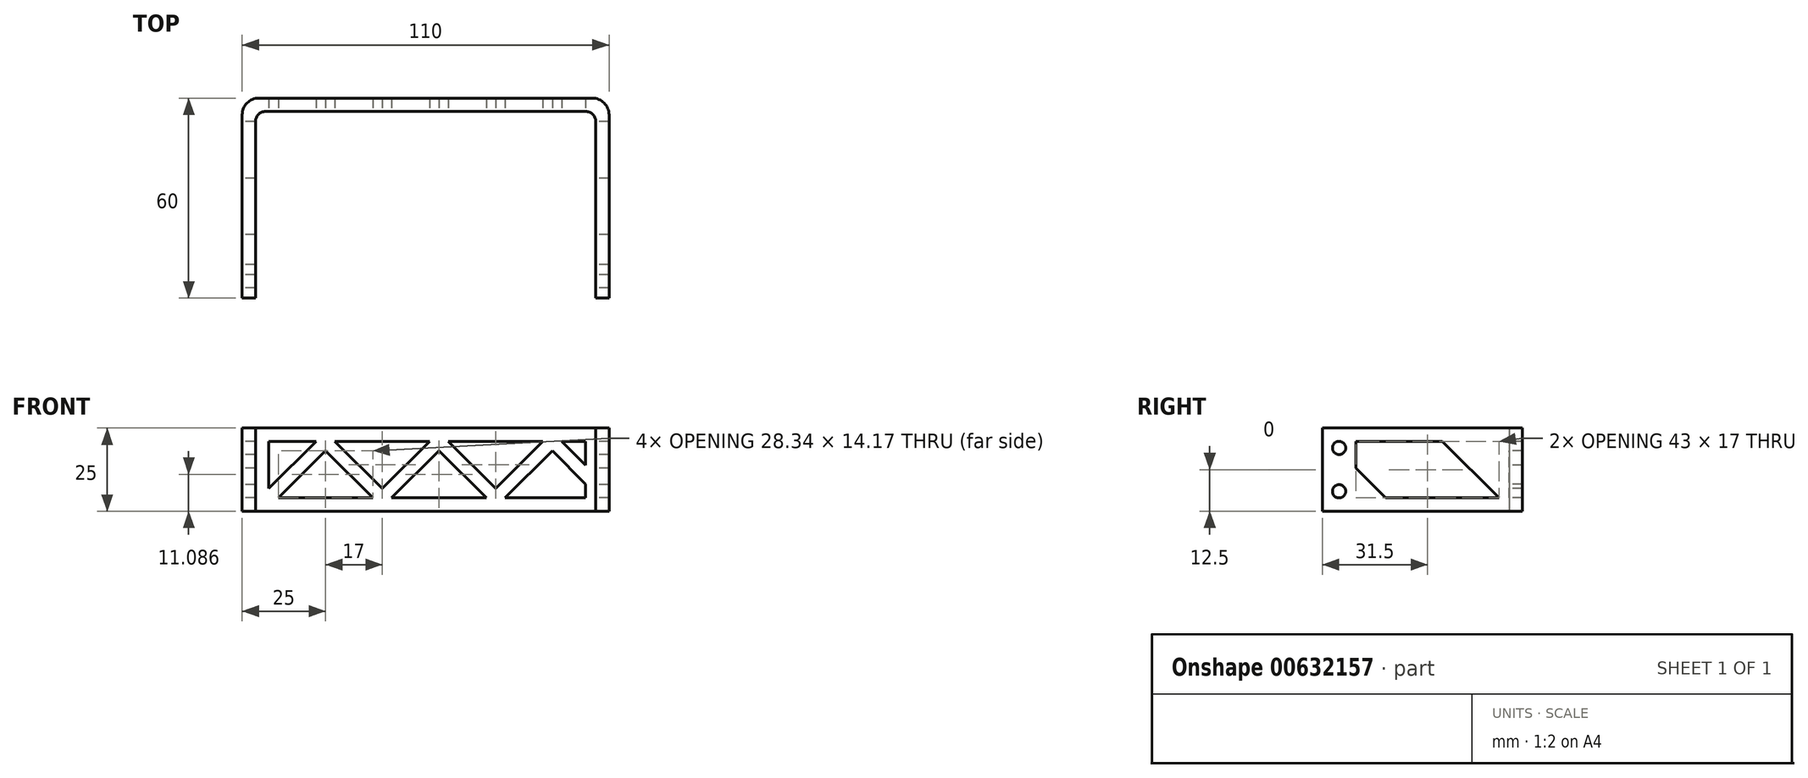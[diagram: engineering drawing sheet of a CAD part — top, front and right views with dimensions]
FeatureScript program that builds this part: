
annotation { "Feature Type Name" : "Feature", "Feature Type Description" : "" }
export const myFeature = defineFeature(function(context is Context, id is Id, definition is map)
    precondition{}
    {
        {
            var Q0;
            Q0=qCreatedBy(makeId("Top.planeOp"),FACE);
            var sketch = newSketch(context, id + "F0", { "sketchPlane" : qUnion([Q0])});
            skLineSegment(sketch, "E0", {"start": v(0, 0) * mm, "end": v(0, 53) * mm});
            skLineSegment(sketch, "E1", {"start": v(-3, 56) * mm, "end": v(-99, 56) * mm});
            skLineSegment(sketch, "E2", {"start": v(-102, 53) * mm, "end": v(-102, 0) * mm});
            skLineSegment(sketch, "E3.0", {"start": v(-106, 55) * mm, "end": v(-106, 0) * mm});
            skLineSegment(sketch, "E3.1", {"start": v(-1, 60) * mm, "end": v(-101, 60) * mm});
            skLineSegment(sketch, "E3.2", {"start": v(4, 0) * mm, "end": v(4, 55) * mm});
            skLineSegment(sketch, "E4.bottom", {"start": v(-106, 0) * mm, "end": v(-102, 0) * mm});
            skLineSegment(sketch, "E5", {"start": v(4, 0) * mm, "end": v(0, 0) * mm});
            skPoint(sketch, "E6.visualSharp", {"position": v(-102, 56) * mm});
            skArc(sketch, "E6.filletArc", {"start": v(-99, 56) * mm, "mid": v(-101.12, 55.12) * mm, "end": v(-102, 53) * mm});
            skPoint(sketch, "E7.visualSharp", {"position": v(0, 56) * mm});
            skArc(sketch, "E7.filletArc", {"start": v(0, 53) * mm, "mid": v(-0.88, 55.12) * mm, "end": v(-3, 56) * mm});
            skPoint(sketch, "E8.visualSharp", {"position": v(-106, 60) * mm});
            skArc(sketch, "E8.filletArc", {"start": v(-101, 60) * mm, "mid": v(-104.54, 58.54) * mm, "end": v(-106, 55) * mm});
            skPoint(sketch, "E9.visualSharp", {"position": v(4, 60) * mm});
            skArc(sketch, "E9.filletArc", {"start": v(4, 55) * mm, "mid": v(2.54, 58.54) * mm, "end": v(-1, 60) * mm});
            skSolve(sketch);
        }
        {
            var Q0;
            Q0=makeQuery(id+"F0.imprint","IMPRINT",FACE,{"disambiguationData":[TD([[makeQuery(id+"F0.imprint","IMPRINT",EDGE,{"derivedFrom":sQuery(id+"F0.wireOp",EDGE,"E0")}),-1.0]])]});
            extrude(context, id + "F1", {"entities" : qUnion([Q0]), "depth" : 25 * mm, "offsetDistance" : 25 * mm});
        }
        {
            var Q0;
            Q0=makeQuery(id+"F1.opExtrude","SWEPT_FACE",FACE,{"disambiguationData":[OSD([sQuery(id+"F0.wireOp",EDGE,"E1")])]});
            var sketch = newSketch(context, id + "F2", { "sketchPlane" : qUnion([Q0])});
            skLineSegment(sketch, "E10", {"start": v(-98, 4) * mm, "end": v(-81, 21) * mm, "construction": true});
            skLineSegment(sketch, "E11", {"start": v(-81, 21) * mm, "end": v(-64, 4) * mm, "construction": true});
            skLineSegment(sketch, "E12", {"start": v(-64, 4) * mm, "end": v(-47, 21) * mm, "construction": true});
            skLineSegment(sketch, "E13", {"start": v(-47, 21) * mm, "end": v(-30, 4) * mm, "construction": true});
            skLineSegment(sketch, "E14", {"start": v(-64, 4) * mm, "end": v(-116.6, 4) * mm, "construction": true});
            skLineSegment(sketch, "E15", {"start": v(-81, 21) * mm, "end": v(-144.6, 21) * mm, "construction": true});
            skLineSegment(sketch, "E16", {"start": v(-64, 4) * mm, "end": v(16.38, 4) * mm, "construction": true});
            skLineSegment(sketch, "E17", {"start": v(-30, 4) * mm, "end": v(-13, 21) * mm, "construction": true});
            skLineSegment(sketch, "E18", {"start": v(-13, 21) * mm, "end": v(-3, 11) * mm, "construction": true});
            skLineSegment(sketch, "E19.0", {"start": v(-13, 18.17) * mm, "end": v(-4.41, 9.59) * mm});
            skLineSegment(sketch, "E19.1", {"start": v(-30, 1.17) * mm, "end": v(-13, 18.17) * mm});
            skLineSegment(sketch, "E19.2", {"start": v(-96.59, 2.59) * mm, "end": v(-81, 18.17) * mm});
            skLineSegment(sketch, "E19.3", {"start": v(-81, 18.17) * mm, "end": v(-64, 1.17) * mm});
            skLineSegment(sketch, "E19.4", {"start": v(-64, 1.17) * mm, "end": v(-47, 18.17) * mm});
            skLineSegment(sketch, "E19.5", {"start": v(-47, 18.17) * mm, "end": v(-30, 1.17) * mm});
            skLineSegment(sketch, "E20.0", {"start": v(-13, 23.83) * mm, "end": v(-1.59, 12.41) * mm});
            skLineSegment(sketch, "E20.1", {"start": v(-30, 6.83) * mm, "end": v(-13, 23.83) * mm});
            skLineSegment(sketch, "E20.2", {"start": v(-99.41, 5.41) * mm, "end": v(-81, 23.83) * mm});
            skLineSegment(sketch, "E20.3", {"start": v(-81, 23.83) * mm, "end": v(-64, 6.83) * mm});
            skLineSegment(sketch, "E20.4", {"start": v(-64, 6.83) * mm, "end": v(-47, 23.83) * mm});
            skLineSegment(sketch, "E20.5", {"start": v(-47, 23.83) * mm, "end": v(-30, 6.83) * mm});
            skLineSegment(sketch, "E21", {"start": v(-98, 4) * mm, "end": v(-64, 4) * mm});
            skLineSegment(sketch, "E22", {"start": v(-30, 4) * mm, "end": v(-3, 4) * mm});
            skLineSegment(sketch, "E23", {"start": v(-3, 4) * mm, "end": v(-3, 11) * mm});
            skLineSegment(sketch, "E24", {"start": v(-81, 21) * mm, "end": v(-47, 21) * mm});
            skLineSegment(sketch, "E25", {"start": v(-13, 21) * mm, "end": v(-47, 21) * mm});
            skLineSegment(sketch, "E26", {"start": v(-13, 21) * mm, "end": v(-3, 21) * mm});
            skLineSegment(sketch, "E27", {"start": v(-3, 21) * mm, "end": v(-3, 11) * mm});
            skLineSegment(sketch, "E28", {"start": v(-98, 4) * mm, "end": v(-98, 21) * mm});
            skLineSegment(sketch, "E29", {"start": v(-98, 21) * mm, "end": v(-81, 21) * mm});
            skLineSegment(sketch, "E30", {"start": v(-64, 4) * mm, "end": v(-30, 4) * mm});
            skLineSegment(sketch, "E31", {"start": v(-4.41, 9.59) * mm, "end": v(-3, 8.17) * mm});
            skSolve(sketch);
        }
        {
            var Q0;
            {var subQ0=sQuery(id+"F2.wireOp",EDGE,"E20.4");var subQ1=sQuery(id+"F2.wireOp",EDGE,"E20.3");var subQ2=makeQuery(id+"F2.imprint","INTERSECT",VERTEX,{"derivedFrom":[subQ1,subQ0]});Q0=makeQuery(id+"F2.imprint","IMPRINT",FACE,{"disambiguationData":[TD([[makeQuery(id+"F2.imprint","IMPRINT",EDGE,{"disambiguationData":[TD([[subQ2,1.0]])],"derivedFrom":subQ1}),1.0]])]});}
            var Q1;
            {var subQ0=sQuery(id+"F2.wireOp",EDGE,"E20.5");var subQ1=sQuery(id+"F2.wireOp",EDGE,"E20.1");var subQ2=makeQuery(id+"F2.imprint","INTERSECT",VERTEX,{"derivedFrom":[subQ1,subQ0]});Q1=makeQuery(id+"F2.imprint","IMPRINT",FACE,{"disambiguationData":[TD([[makeQuery(id+"F2.imprint","IMPRINT",EDGE,{"disambiguationData":[TD([[subQ2,-1.0]])],"derivedFrom":subQ1}),1.0]])]});}
            var Q2;
            {var subQ0=sQuery(id+"F2.wireOp",EDGE,"E19.3");var subQ1=sQuery(id+"F2.wireOp",EDGE,"E19.2");var subQ2=makeQuery(id+"F2.imprint","INTERSECT",VERTEX,{"derivedFrom":[subQ1,subQ0]});Q2=makeQuery(id+"F2.imprint","IMPRINT",FACE,{"disambiguationData":[TD([[makeQuery(id+"F2.imprint","IMPRINT",EDGE,{"disambiguationData":[TD([[subQ2,1.0]])],"derivedFrom":subQ1}),-1.0]])]});}
            var Q3;
            {var subQ0=sQuery(id+"F2.wireOp",EDGE,"E27");var subQ1=sQuery(id+"F2.wireOp",EDGE,"E20.0");var subQ2=makeQuery(id+"F2.imprint","INTERSECT",VERTEX,{"derivedFrom":[subQ1,subQ0]});Q3=makeQuery(id+"F2.imprint","IMPRINT",FACE,{"disambiguationData":[TD([[makeQuery(id+"F2.imprint","IMPRINT",EDGE,{"disambiguationData":[TD([[subQ2,1.0]])],"derivedFrom":subQ1}),1.0]])]});}
            var Q4;
            {var subQ0=sQuery(id+"F2.wireOp",EDGE,"E28");var subQ1=sQuery(id+"F2.wireOp",EDGE,"E20.2");var subQ2=makeQuery(id+"F2.imprint","INTERSECT",VERTEX,{"derivedFrom":[subQ1,subQ0]});Q4=makeQuery(id+"F2.imprint","IMPRINT",FACE,{"disambiguationData":[TD([[makeQuery(id+"F2.imprint","IMPRINT",EDGE,{"disambiguationData":[TD([[subQ2,-1.0]])],"derivedFrom":subQ1}),1.0]])]});}
            var Q5;
            {var subQ0=sQuery(id+"F2.wireOp",EDGE,"E19.5");var subQ1=sQuery(id+"F2.wireOp",EDGE,"E19.4");var subQ2=makeQuery(id+"F2.imprint","INTERSECT",VERTEX,{"derivedFrom":[subQ1,subQ0]});Q5=makeQuery(id+"F2.imprint","IMPRINT",FACE,{"disambiguationData":[TD([[makeQuery(id+"F2.imprint","IMPRINT",EDGE,{"disambiguationData":[TD([[subQ2,1.0]])],"derivedFrom":subQ1}),-1.0]])]});}
            var Q6;
            {var subQ6=sQuery(id+"F2.wireOp",EDGE,"E19.0");Q6=makeQuery(id+"F2.imprint","IMPRINT",FACE,{"disambiguationData":[TD([[makeQuery(id+"F2.imprint","IMPRINT",EDGE,{"derivedFrom":subQ6}),-1.0]])]});}
            extrude(context, id + "F3", {"entities" : qUnion([Q0, Q1, Q2, Q3, Q4, Q5, Q6]), "operationType" : NewBodyOperationType.REMOVE, "oppositeDirection" : true, "depth" : 25 * mm, "offsetDistance" : 25 * mm});
        }
        {
            var Q0;
            Q0=makeQuery(id+"F1.opExtrude","SWEPT_FACE",FACE,{"disambiguationData":[OSD([sQuery(id+"F0.wireOp",EDGE,"E3.0")])]});
            var sketch = newSketch(context, id + "F4", { "sketchPlane" : qUnion([Q0])});
            skCircle(sketch, "E32", {"center": v(-5, 19) * mm, "radius": 2 * mm});
            skCircle(sketch, "E33", {"center": v(-5, 6) * mm, "radius": 2 * mm});
            skLineSegment(sketch, "E34", {"start": v(-5, 19) * mm, "end": v(-5, 6) * mm, "construction": true});
            skLineSegment(sketch, "E35", {"start": v(0, 21) * mm, "end": v(-60.34, 21) * mm});
            skLineSegment(sketch, "E36", {"start": v(0, 4) * mm, "end": v(-60.1, 4) * mm});
            skLineSegment(sketch, "E37", {"start": v(-53, 4) * mm, "end": v(-36, 21) * mm});
            skLineSegment(sketch, "E38", {"start": v(-36, 21) * mm, "end": v(-19, 4) * mm});
            skLineSegment(sketch, "E39", {"start": v(-10, 4) * mm, "end": v(-10, 21) * mm});
            skLineSegment(sketch, "E40", {"start": v(-19, 4) * mm, "end": v(-10, 13) * mm});
            skSolve(sketch);
        }
        {
            var Q0;
            Q0=makeQuery(id+"F4.imprint","IMPRINT",FACE,{"disambiguationData":[TD([[makeQuery(id+"F4.imprint","IMPRINT",EDGE,{"derivedFrom":sQuery(id+"F4.wireOp",EDGE,"E32")}),1.0]])]});
            var Q1;
            Q1=makeQuery(id+"F4.imprint","IMPRINT",FACE,{"disambiguationData":[TD([[makeQuery(id+"F4.imprint","IMPRINT",EDGE,{"derivedFrom":sQuery(id+"F4.wireOp",EDGE,"E33")}),1.0]])]});
            var Q2;
            {var subQ0=sQuery(id+"F4.wireOp",EDGE,"E38");Q2=makeQuery(id+"F4.imprint","IMPRINT",FACE,{"disambiguationData":[TD([[makeQuery(id+"F4.imprint","IMPRINT",EDGE,{"derivedFrom":subQ0}),1.0]])]});}
            var Q3;
            {var subQ0=sQuery(id+"F4.wireOp",EDGE,"E37");Q3=makeQuery(id+"F4.imprint","IMPRINT",FACE,{"disambiguationData":[TD([[makeQuery(id+"F4.imprint","IMPRINT",EDGE,{"derivedFrom":subQ0}),-1.0]])]});}
            extrude(context, id + "F5", {"entities" : qUnion([Q0, Q1, Q2, Q3]), "operationType" : NewBodyOperationType.REMOVE, "oppositeDirection" : true, "depth" : 200 * mm, "offsetDistance" : 25 * mm});
        }
    });
